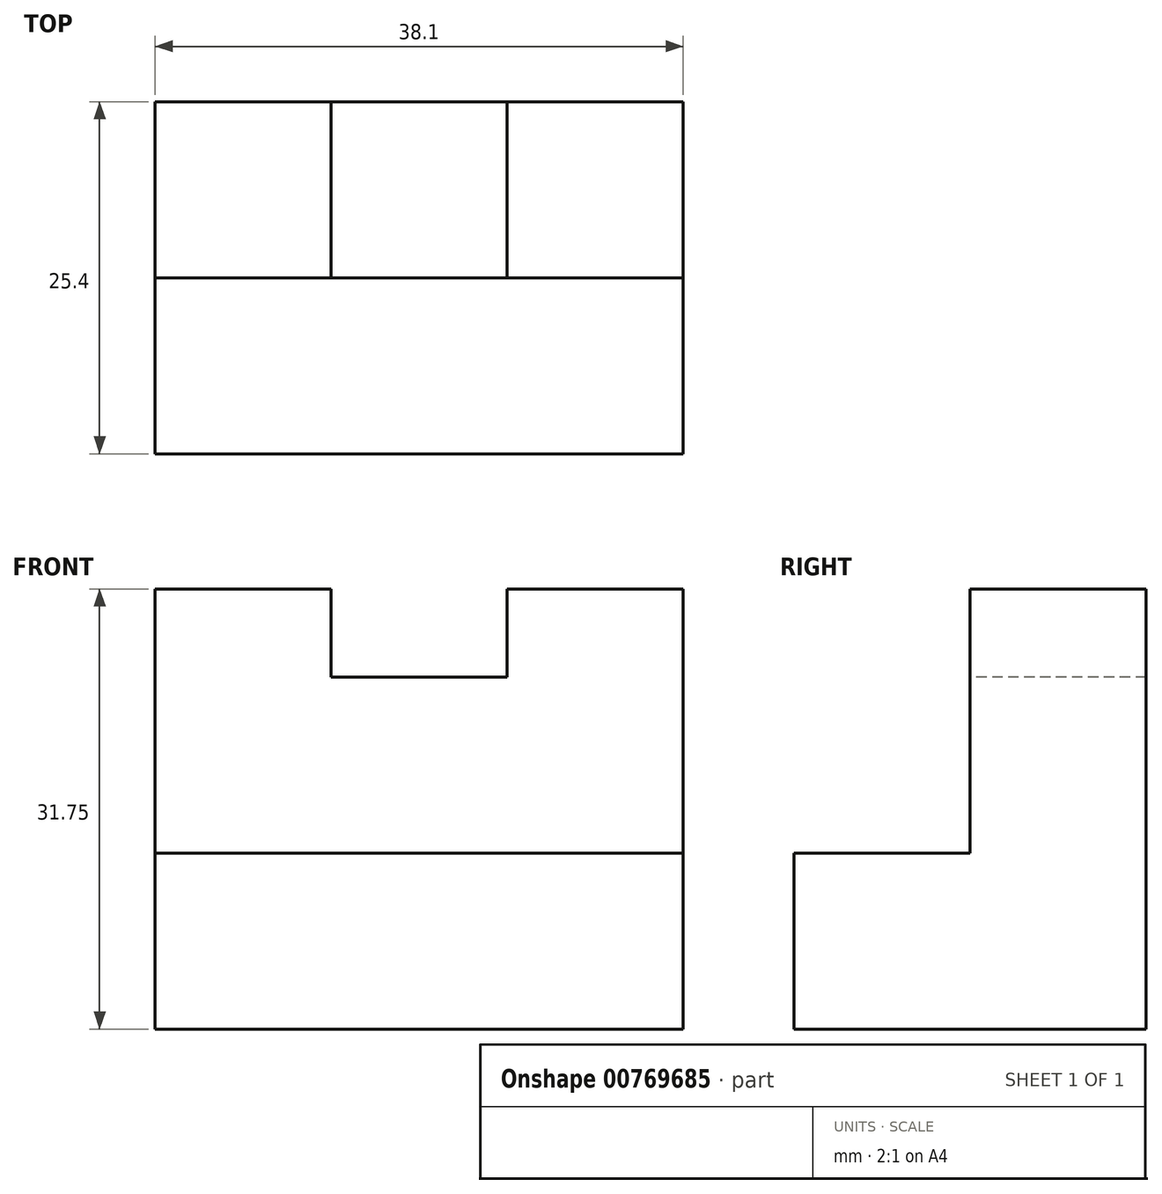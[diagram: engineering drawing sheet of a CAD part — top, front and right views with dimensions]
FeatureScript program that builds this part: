
annotation { "Feature Type Name" : "Feature", "Feature Type Description" : "" }
export const myFeature = defineFeature(function(context is Context, id is Id, definition is map)
    precondition{}
    {
        {
            var Q0;
            Q0=qCreatedBy(makeId("Right.planeOp"),FACE);
            var sketch = newSketch(context, id + "F0", { "sketchPlane" : qUnion([Q0])});
            skLineSegment(sketch, "E0", {"start": v(0, 0) * mm, "end": v(25.4, 0) * mm});
            skLineSegment(sketch, "E1", {"start": v(25.4, 0) * mm, "end": v(25.4, 31.75) * mm});
            skLineSegment(sketch, "E2", {"start": v(25.4, 31.75) * mm, "end": v(12.7, 31.75) * mm});
            skLineSegment(sketch, "E3", {"start": v(12.7, 31.75) * mm, "end": v(12.7, 12.7) * mm});
            skLineSegment(sketch, "E4", {"start": v(12.7, 12.7) * mm, "end": v(0, 12.7) * mm});
            skLineSegment(sketch, "E5", {"start": v(0, 12.7) * mm, "end": v(0, 0) * mm});
            skSolve(sketch);
        }
        {
            var Q0;
            Q0 = qSketchRegion(id + "F0", true);
            var Q1;
            Q1=makeQuery(id+"F0.imprint","IMPRINT",FACE,{"disambiguationData":[TD([[makeQuery(id+"F0.imprint","IMPRINT",EDGE,{"derivedFrom":sQuery(id+"F0.wireOp",EDGE,"E0")}),1.0]])]});
            extrude(context, id + "F1", {"entities" : qUnion([Q0, Q1]), "depth" : 38.1 * mm, "offsetDistance" : 25.4 * mm});
        }
        {
            var Q0;
            Q0=makeQuery(id+"F1.opExtrude","SWEPT_FACE",FACE,{"disambiguationData":[OSD([sQuery(id+"F0.wireOp",EDGE,"E3")])]});
            var sketch = newSketch(context, id + "F2", { "sketchPlane" : qUnion([Q0])});
            skLineSegment(sketch, "E6", {"start": v(0, 31.75) * mm, "end": v(12.7, 31.75) * mm});
            skLineSegment(sketch, "E7", {"start": v(12.7, 31.75) * mm, "end": v(12.7, 25.4) * mm});
            skLineSegment(sketch, "E8.bottom", {"start": v(12.7, 31.75) * mm, "end": v(25.4, 31.75) * mm});
            skLineSegment(sketch, "E8.top", {"start": v(12.7, 25.4) * mm, "end": v(25.4, 25.4) * mm});
            skLineSegment(sketch, "E8.right", {"start": v(25.4, 31.75) * mm, "end": v(25.4, 25.4) * mm});
            skSolve(sketch);
        }
        {
            var Q0;
            Q0 = qSketchRegion(id + "F2", true);
            extrude(context, id + "F3", {"entities" : qUnion([Q0]), "operationType" : NewBodyOperationType.REMOVE, "oppositeDirection" : true, "depth" : 25.4 * mm, "offsetDistance" : 25.4 * mm});
        }
    });
